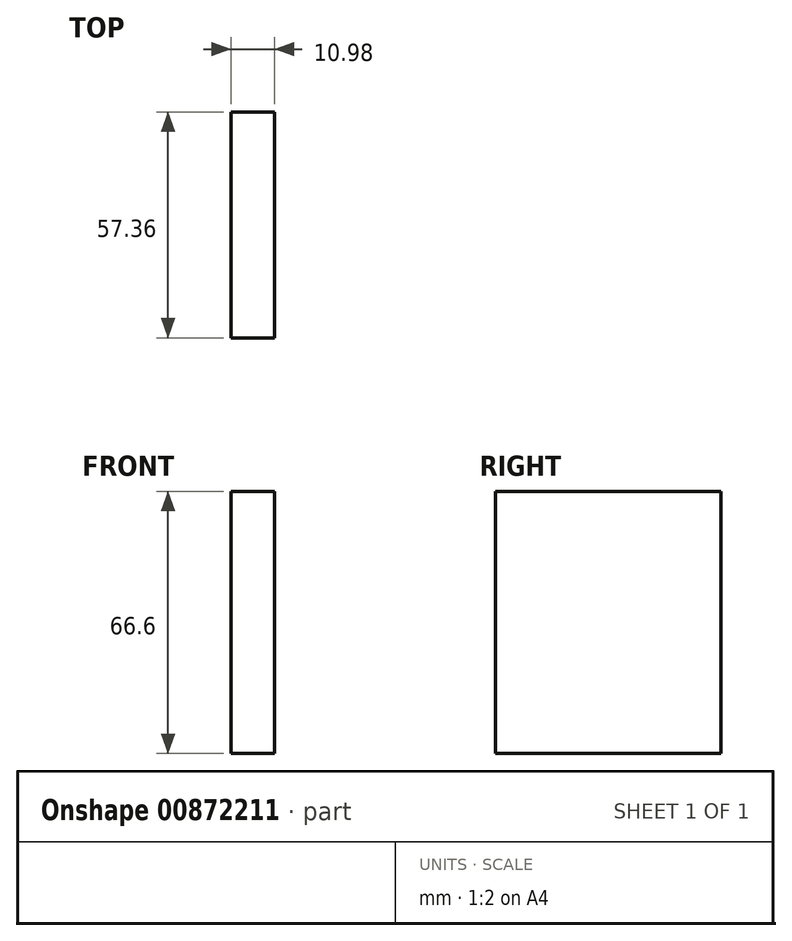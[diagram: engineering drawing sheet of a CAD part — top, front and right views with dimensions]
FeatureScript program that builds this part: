
annotation { "Feature Type Name" : "Feature", "Feature Type Description" : "" }
export const myFeature = defineFeature(function(context is Context, id is Id, definition is map)
    precondition{}
    {
        {
            var Q0;
            Q0=qCreatedBy(makeId("Front.planeOp"),FACE);
            var sketch = newSketch(context, id + "F0", { "sketchPlane" : qUnion([Q0])});
            skLineSegment(sketch, "E0.bottom", {"start": v(-31.13, 0) * mm, "end": v(-20.15, 0) * mm});
            skLineSegment(sketch, "E0.top", {"start": v(-31.13, 66.6) * mm, "end": v(-20.15, 66.6) * mm});
            skLineSegment(sketch, "E0.left", {"start": v(-31.13, 0) * mm, "end": v(-31.13, 66.6) * mm});
            skLineSegment(sketch, "E0.right", {"start": v(-20.15, 0) * mm, "end": v(-20.15, 66.6) * mm});
            skSolve(sketch);
        }
        {
            var Q0;
            Q0=makeQuery(id+"F0.imprint","IMPRINT",FACE,{"disambiguationData":[TD([[makeQuery(id+"F0.imprint","IMPRINT",EDGE,{"derivedFrom":sQuery(id+"F0.wireOp",EDGE,"E0.bottom")}),1.0]])]});
            extrude(context, id + "F1", {"entities" : qUnion([Q0]), "depth" : 57.36 * mm, "offsetDistance" : 25.4 * mm});
        }
    });
